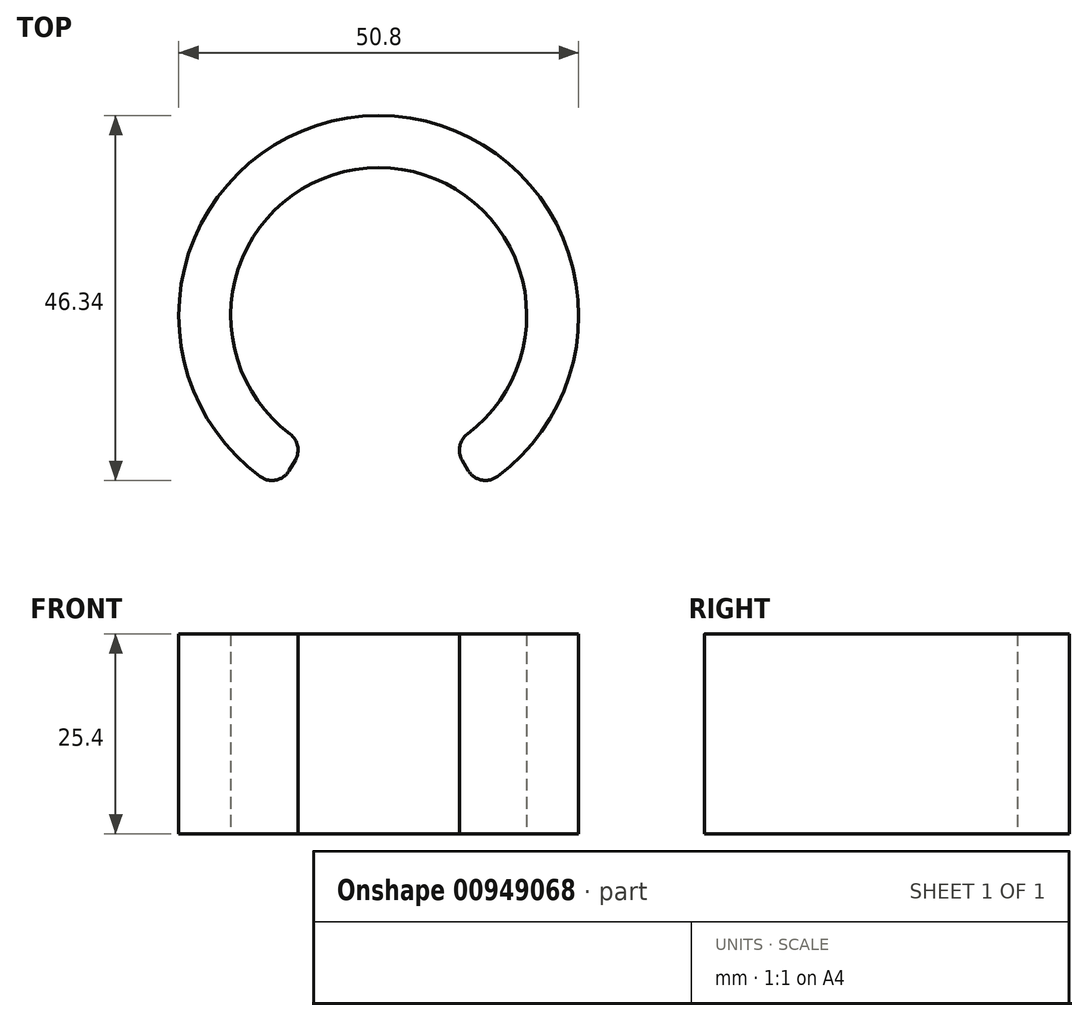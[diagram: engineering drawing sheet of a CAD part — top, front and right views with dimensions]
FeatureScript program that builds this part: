
annotation { "Feature Type Name" : "Feature", "Feature Type Description" : "" }
export const myFeature = defineFeature(function(context is Context, id is Id, definition is map)
    precondition{}
    {
        {
            var Q0;
            Q0=qCreatedBy(makeId("Top.planeOp"),FACE);
            var sketch = newSketch(context, id + "F0", { "sketchPlane" : qUnion([Q0])});
            skArc(sketch, "E0", {"start": v(11.27, -15.04) * mm, "mid": v(0, 18.8) * mm, "end": v(-11.27, -15.04) * mm});
            skArc(sketch, "E1", {"start": v(15.07, -20.45) * mm, "mid": v(0, 25.4) * mm, "end": v(-15.07, -20.45) * mm});
            skLineSegment(sketch, "E2", {"start": v(-10.6, -18.35) * mm, "end": v(-11.36, -19.67) * mm});
            skLineSegment(sketch, "E3", {"start": v(0, 0) * mm, "end": v(0, -25.4) * mm, "construction": true});
            skLineSegment(sketch, "E4.MirrorCS", {"start": v(10.6, -18.35) * mm, "end": v(11.36, -19.67) * mm});
            skPoint(sketch, "E5.visualSharp", {"position": v(-9.4, -16.28) * mm});
            skArc(sketch, "E5.filletArc", {"start": v(-10.6, -18.35) * mm, "mid": v(-10.3, -16.57) * mm, "end": v(-11.27, -15.04) * mm});
            skPoint(sketch, "E6.visualSharp", {"position": v(-12.7, -22) * mm});
            skArc(sketch, "E6.filletArc", {"start": v(-15.07, -20.45) * mm, "mid": v(-13.04, -20.9) * mm, "end": v(-11.36, -19.67) * mm});
            skPoint(sketch, "E7.visualSharp", {"position": v(9.4, -16.28) * mm});
            skArc(sketch, "E7.filletArc", {"start": v(11.27, -15.04) * mm, "mid": v(10.3, -16.57) * mm, "end": v(10.6, -18.35) * mm});
            skPoint(sketch, "E8.visualSharp", {"position": v(12.7, -22) * mm});
            skArc(sketch, "E8.filletArc", {"start": v(11.36, -19.67) * mm, "mid": v(13.04, -20.9) * mm, "end": v(15.07, -20.45) * mm});
            skSolve(sketch);
        }
        {
            var Q0;
            Q0=makeQuery(id+"F0.imprint","IMPRINT",FACE,{"disambiguationData":[TD([[makeQuery(id+"F0.imprint","IMPRINT",EDGE,{"derivedFrom":sQuery(id+"F0.wireOp",EDGE,"E0")}),-1.0]])]});
            extrude(context, id + "F1", {"entities" : qUnion([Q0]), "depth" : 25.4 * mm, "offsetDistance" : 25.4 * mm});
        }
    });
